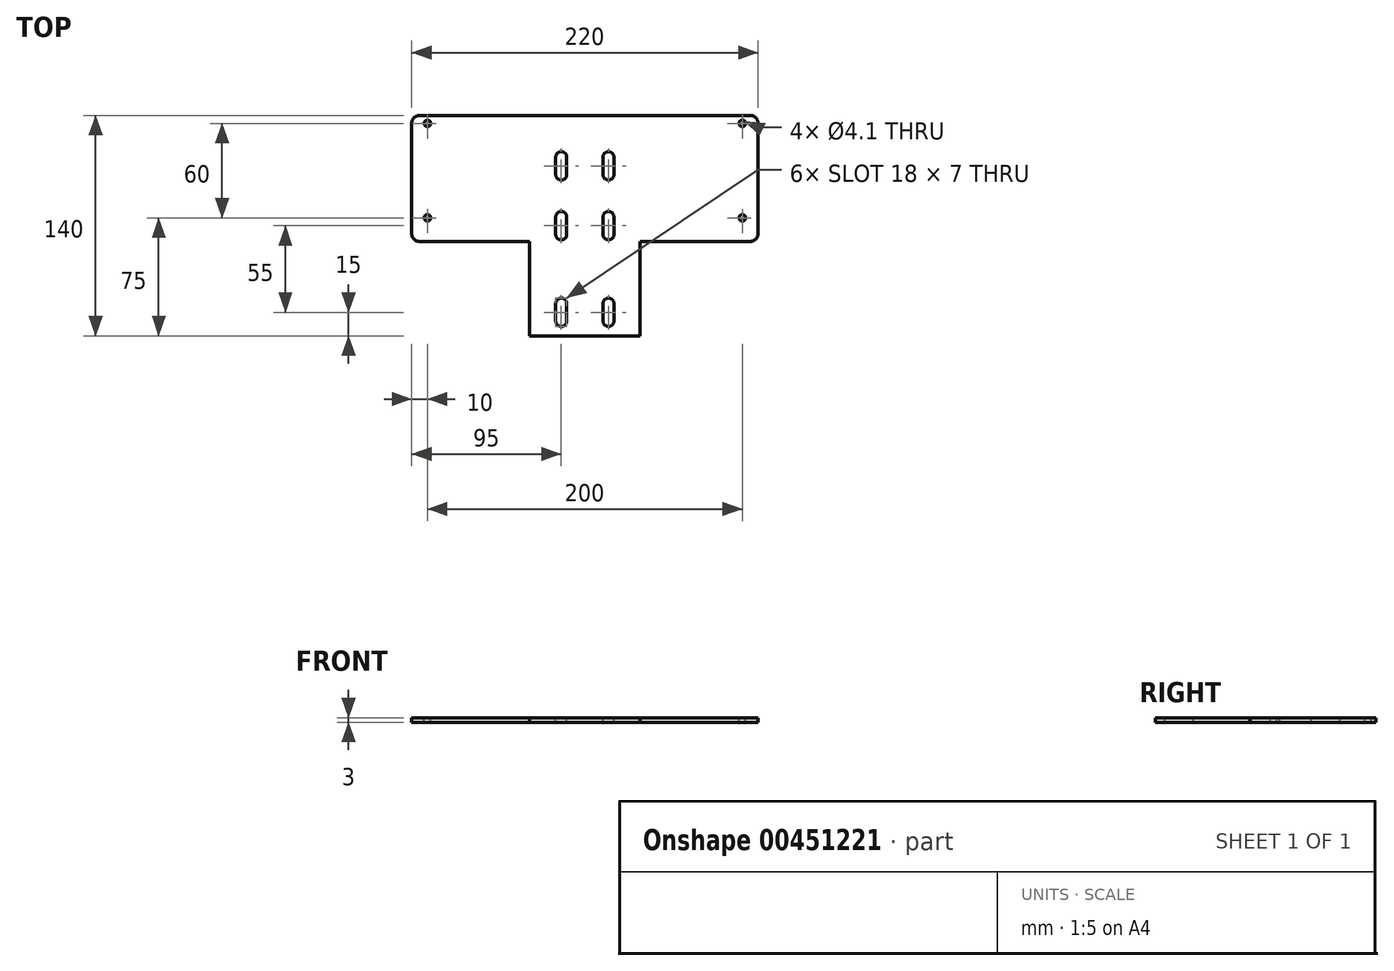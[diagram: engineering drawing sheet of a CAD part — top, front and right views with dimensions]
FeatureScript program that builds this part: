
annotation { "Feature Type Name" : "Feature", "Feature Type Description" : "" }
export const myFeature = defineFeature(function(context is Context, id is Id, definition is map)
    precondition{}
    {
        {
            var Q0;
            Q0=qCreatedBy(makeId("Top.planeOp"),FACE);
            var sketch = newSketch(context, id + "F0", { "sketchPlane" : qUnion([Q0])});
            skLineSegment(sketch, "E0.bottom", {"start": v(110, -15) * mm, "end": v(-110, -15) * mm});
            skLineSegment(sketch, "E0.top", {"start": v(110, 15) * mm, "end": v(-110, 15) * mm});
            skLineSegment(sketch, "E0.left", {"start": v(110, -15) * mm, "end": v(110, 15) * mm});
            skLineSegment(sketch, "E0.right", {"start": v(-110, -15) * mm, "end": v(-110, 15) * mm});
            skPoint(sketch, "E0.middle", {"position": v(0, 0) * mm});
            skLineSegment(sketch, "E1.bottom", {"start": v(35, -75) * mm, "end": v(-35, -75) * mm});
            skLineSegment(sketch, "E1.top", {"start": v(35, -15) * mm, "end": v(-35, -15) * mm});
            skLineSegment(sketch, "E1.left", {"start": v(35, -75) * mm, "end": v(35, -15) * mm});
            skLineSegment(sketch, "E1.right", {"start": v(-35, -75) * mm, "end": v(-35, -15) * mm});
            skPoint(sketch, "E1.middle", {"position": v(0, -45) * mm});
            skLineSegment(sketch, "E2.bottom", {"start": v(-110, 65) * mm, "end": v(110, 65) * mm});
            skLineSegment(sketch, "E3", {"start": v(-110, 65) * mm, "end": v(-110, 15) * mm});
            skLineSegment(sketch, "E4", {"start": v(110, 65) * mm, "end": v(110, 15) * mm});
            skSolve(sketch);
        }
        {
            var Q0;
            Q0 = qSketchRegion(id + "F0", true);
            extrude(context, id + "F1", {"entities" : qUnion([Q0]), "depth" : 3 * mm, "offsetDistance" : 25 * mm});
        }
        {
            var Q0;
            Q0=makeQuery(id+"F1.opExtrude","CAP_FACE",FACE,{"disambiguationData":[OSD([sQuery(id+"F0.wireOp",EDGE,"E0.bottom"),sQuery(id+"F0.wireOp",EDGE,"E0.top"),sQuery(id+"F0.wireOp",EDGE,"E0.left"),sQuery(id+"F0.wireOp",EDGE,"E0.right")])],"isStart":false});
            var sketch = newSketch(context, id + "F2", { "sketchPlane" : qUnion([Q0])});
            skCircle(sketch, "E5", {"center": v(-100, 0) * mm, "radius": 2.05 * mm});
            skCircle(sketch, "E6", {"center": v(100, 0) * mm, "radius": 2.05 * mm});
            skLineSegment(sketch, "E7.bottom", {"start": v(-11.5, 27.5) * mm, "end": v(-18.5, 27.5) * mm, "construction": true});
            skLineSegment(sketch, "E7.top", {"start": v(-11.5, 38.5) * mm, "end": v(-18.5, 38.5) * mm, "construction": true});
            skLineSegment(sketch, "E7.left", {"start": v(-11.5, 27.5) * mm, "end": v(-11.5, 38.5) * mm});
            skLineSegment(sketch, "E7.right", {"start": v(-18.5, 27.5) * mm, "end": v(-18.5, 38.5) * mm});
            skPoint(sketch, "E7.middle", {"position": v(-15, 33) * mm});
            skArc(sketch, "E8", {"start": v(-11.5, 38.5) * mm, "mid": v(-15, 42) * mm, "end": v(-18.5, 38.5) * mm});
            skArc(sketch, "E9", {"start": v(-18.5, 27.5) * mm, "mid": v(-15, 24) * mm, "end": v(-11.5, 27.5) * mm});
            skLineSegment(sketch, "E10.bottom", {"start": v(18.5, 27.5) * mm, "end": v(11.5, 27.5) * mm, "construction": true});
            skLineSegment(sketch, "E10.top", {"start": v(18.5, 38.5) * mm, "end": v(11.5, 38.5) * mm, "construction": true});
            skLineSegment(sketch, "E10.left", {"start": v(18.5, 27.5) * mm, "end": v(18.5, 38.5) * mm});
            skLineSegment(sketch, "E10.right", {"start": v(11.5, 27.5) * mm, "end": v(11.5, 38.5) * mm});
            skPoint(sketch, "E10.middle", {"position": v(15, 33) * mm});
            skArc(sketch, "E11", {"start": v(18.5, 38.5) * mm, "mid": v(15, 42) * mm, "end": v(11.5, 38.5) * mm});
            skArc(sketch, "E12", {"start": v(11.5, 27.5) * mm, "mid": v(15, 24) * mm, "end": v(18.5, 27.5) * mm});
            skLineSegment(sketch, "E13.bottom", {"start": v(-11.5, -65.5) * mm, "end": v(-18.5, -65.5) * mm, "construction": true});
            skLineSegment(sketch, "E13.top", {"start": v(-11.5, -54.5) * mm, "end": v(-18.5, -54.5) * mm, "construction": true});
            skLineSegment(sketch, "E13.left", {"start": v(-11.5, -65.5) * mm, "end": v(-11.5, -54.5) * mm});
            skLineSegment(sketch, "E13.right", {"start": v(-18.5, -65.5) * mm, "end": v(-18.5, -54.5) * mm});
            skPoint(sketch, "E13.middle", {"position": v(-15, -60) * mm});
            skArc(sketch, "E14", {"start": v(-11.5, -54.5) * mm, "mid": v(-15, -51) * mm, "end": v(-18.5, -54.5) * mm});
            skArc(sketch, "E15", {"start": v(-18.5, -65.5) * mm, "mid": v(-15, -69) * mm, "end": v(-11.5, -65.5) * mm});
            skLineSegment(sketch, "E16.bottom", {"start": v(18.5, -65.5) * mm, "end": v(11.5, -65.5) * mm, "construction": true});
            skLineSegment(sketch, "E16.top", {"start": v(18.5, -54.5) * mm, "end": v(11.5, -54.5) * mm, "construction": true});
            skLineSegment(sketch, "E16.left", {"start": v(18.5, -65.5) * mm, "end": v(18.5, -54.5) * mm});
            skLineSegment(sketch, "E16.right", {"start": v(11.5, -65.5) * mm, "end": v(11.5, -54.5) * mm});
            skPoint(sketch, "E16.middle", {"position": v(15, -60) * mm});
            skArc(sketch, "E17", {"start": v(18.5, -54.5) * mm, "mid": v(15, -51) * mm, "end": v(11.5, -54.5) * mm});
            skArc(sketch, "E18", {"start": v(11.5, -65.5) * mm, "mid": v(15, -69) * mm, "end": v(18.5, -65.5) * mm});
            skCircle(sketch, "E19", {"center": v(-100, 60) * mm, "radius": 2.05 * mm});
            skCircle(sketch, "E20", {"center": v(100, 60) * mm, "radius": 2.05 * mm});
            skLineSegment(sketch, "E21.bottom", {"start": v(-11.5, -10.5) * mm, "end": v(-18.5, -10.5) * mm, "construction": true});
            skLineSegment(sketch, "E21.top", {"start": v(-11.5, 0.5) * mm, "end": v(-18.5, 0.5) * mm, "construction": true});
            skLineSegment(sketch, "E21.left", {"start": v(-11.5, -10.5) * mm, "end": v(-11.5, 0.5) * mm});
            skLineSegment(sketch, "E21.right", {"start": v(-18.5, -10.5) * mm, "end": v(-18.5, 0.5) * mm});
            skPoint(sketch, "E21.middle", {"position": v(-15, -5) * mm});
            skArc(sketch, "E22", {"start": v(-11.5, 0.5) * mm, "mid": v(-15, 4) * mm, "end": v(-18.5, 0.5) * mm});
            skArc(sketch, "E23", {"start": v(-18.5, -10.5) * mm, "mid": v(-15, -14) * mm, "end": v(-11.5, -10.5) * mm});
            skLineSegment(sketch, "E24.bottom", {"start": v(18.5, -10.5) * mm, "end": v(11.5, -10.5) * mm, "construction": true});
            skLineSegment(sketch, "E24.top", {"start": v(18.5, 0.5) * mm, "end": v(11.5, 0.5) * mm, "construction": true});
            skLineSegment(sketch, "E24.left", {"start": v(18.5, -10.5) * mm, "end": v(18.5, 0.5) * mm});
            skLineSegment(sketch, "E24.right", {"start": v(11.5, -10.5) * mm, "end": v(11.5, 0.5) * mm});
            skPoint(sketch, "E24.middle", {"position": v(15, -5) * mm});
            skArc(sketch, "E25", {"start": v(18.5, 0.5) * mm, "mid": v(15, 4) * mm, "end": v(11.5, 0.5) * mm});
            skArc(sketch, "E26", {"start": v(11.5, -10.5) * mm, "mid": v(15, -14) * mm, "end": v(18.5, -10.5) * mm});
            skSolve(sketch);
        }
        {
            var Q0;
            Q0=qSketchRegion(id+"F2",true);
            extrude(context, id + "F3", {"entities" : qUnion([Q0]), "operationType" : NewBodyOperationType.REMOVE, "oppositeDirection" : true, "depth" : 25 * mm, "offsetDistance" : 25 * mm});
        }
        {
            var Q0;
            Q0=makeQuery(id+"F1.opExtrude","SWEPT_EDGE",EDGE,{"disambiguationData":[OSD([sQuery(id+"F0.wireOp",EDGE,"E0.bottom"),sQuery(id+"F0.wireOp",EDGE,"E0.right")])]});
            var Q1;
            Q1=makeQuery(id+"F1.opExtrude","SWEPT_EDGE",EDGE,{"disambiguationData":[OSD([sQuery(id+"F0.wireOp",EDGE,"E0.top"),sQuery(id+"F0.wireOp",EDGE,"E0.right")])]});
            var Q2;
            Q2=makeQuery(id+"F1.opExtrude","SWEPT_EDGE",EDGE,{"disambiguationData":[OSD([sQuery(id+"F0.wireOp",EDGE,"E0.bottom"),sQuery(id+"F0.wireOp",EDGE,"E0.left")])]});
            var Q3;
            Q3=makeQuery(id+"F1.opExtrude","SWEPT_EDGE",EDGE,{"disambiguationData":[OSD([sQuery(id+"F0.wireOp",EDGE,"E0.top"),sQuery(id+"F0.wireOp",EDGE,"E0.left")])]});
            var Q4;
            Q4=makeQuery(id+"F1.opExtrude","SWEPT_EDGE",EDGE,{"disambiguationData":[OSD([sQuery(id+"F0.wireOp",EDGE,"E2.top"),sQuery(id+"F0.wireOp",EDGE,"E2.right")])]});
            var Q5;
            Q5=makeQuery(id+"F1.opExtrude","SWEPT_EDGE",EDGE,{"disambiguationData":[OSD([sQuery(id+"F0.wireOp",EDGE,"E2.bottom"),sQuery(id+"F0.wireOp",EDGE,"E2.right")])]});
            var Q6;
            Q6=makeQuery(id+"F1.opExtrude","SWEPT_EDGE",EDGE,{"disambiguationData":[OSD([sQuery(id+"F0.wireOp",EDGE,"E2.top"),sQuery(id+"F0.wireOp",EDGE,"E2.left")])]});
            var Q7;
            Q7=makeQuery(id+"F1.opExtrude","SWEPT_EDGE",EDGE,{"disambiguationData":[OSD([sQuery(id+"F0.wireOp",EDGE,"E2.bottom"),sQuery(id+"F0.wireOp",EDGE,"E2.left")])]});
            fillet(context, id + "F4", {"entities" : qUnion([Q0, Q1, Q2, Q3, Q4, Q5, Q6, Q7]), "radius" : 5 * mm, "tangentPropagation" : true, "allowEdgeOverflow" : false});
        }
    });
